# Revit family: 0925Y
name_source: partatom
category: Mechanical Equipment
revit_build: Autodesk Revit 2018 (Build: 20170223_1515(x64)
units: mm (PartAtom-declared; Revit-internal decimal feet)

## family parameters
Always vertical = No
Classification = None
Cut with Voids When Loaded = No
OmniClass Number = 23.45.05.21
OmniClass Title = Plumbing Fixtures - Sanitary Disposal Units
Part Type = Normal
Room Calculation Point = No
Round Connector Dimension = Use Diameter
Shared = Yes
Work Plane-Based = Yes

## types (1)
- 0925Y
    Base Depth from Finished Floor = 2"
    C Dimensions (3" Min to 4-1/2" Max) = 3"
    Default Elevation = 0"
    Description = LABOR SAVER® HEAVY DUTY FIXTURE SUPPORT FLOOR MOUNTED
    Fitting Height = 22 23/32"
    Manufacturer = Jay R. Smith
    Material = Metal-Jay R. Smith-Cast Iron
    Model = 0925Y
    No-Hub Waste Fitting Radius = 2"
    No-Hub Waste Fitting Size = 4"
    Outlet Connection Radius = 2"
    Outlet Connection Size = 4"
    Price = Prices may vary. Please consult Manufacturer Representative for most up-to-date price list.
    Product Documentation Link = https://www.jrsmith.com
    Product Page URL = https://www.jrsmith.com
    Stud Height = 40"
    URL = https://www.jrsmith.com
    Vent Connection Radius = 2"
    Vent Connection Size = 4"

## geometry (parser evidence)
native form markers: Sweep x9
no freeform markers — native parametric forms only
